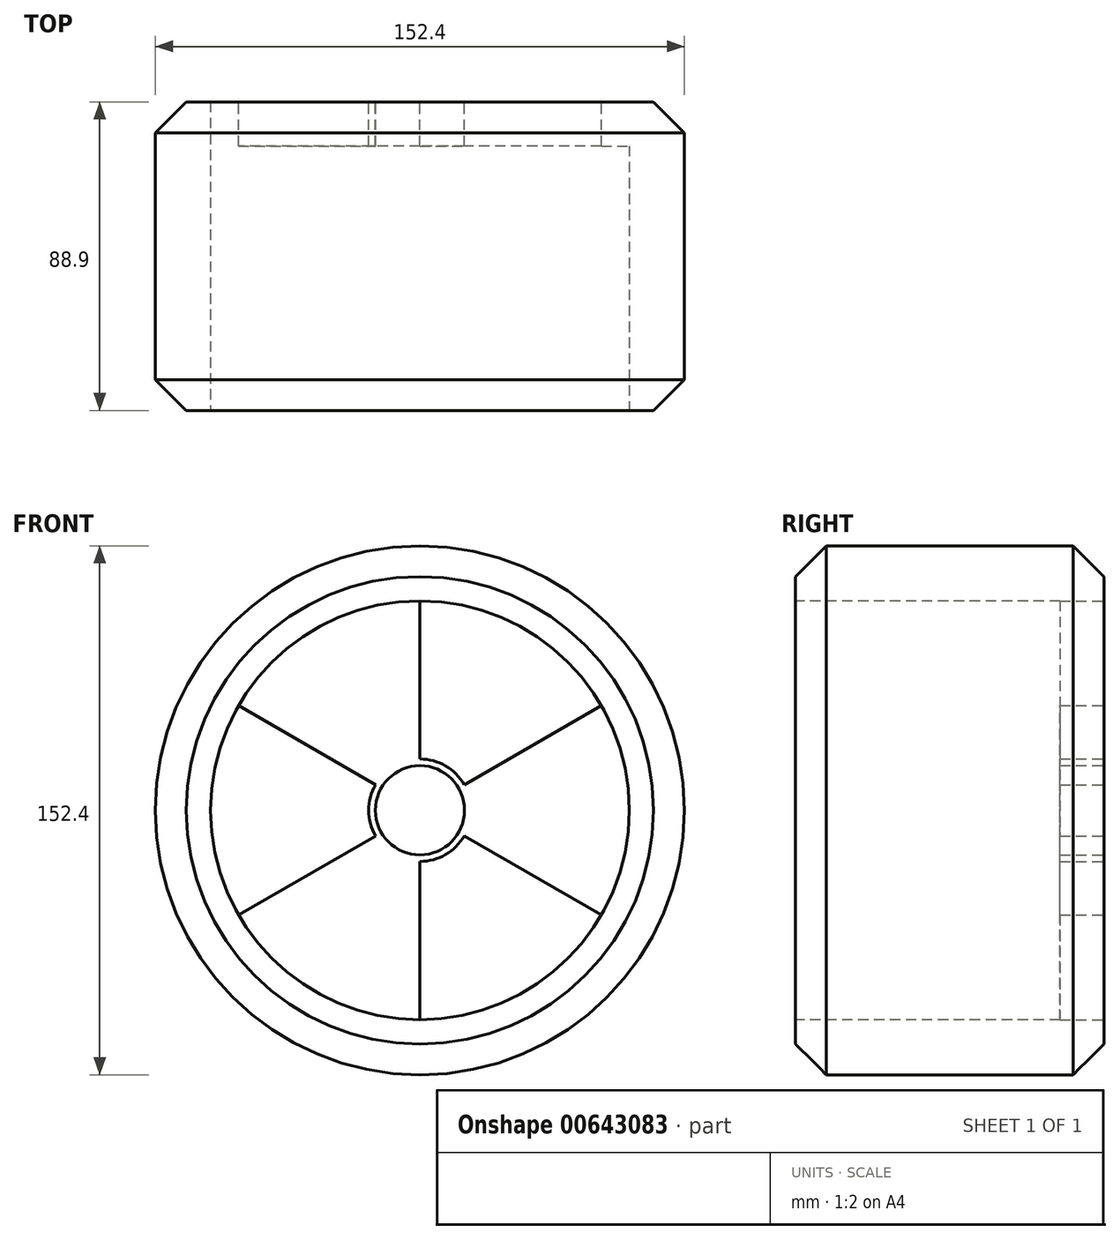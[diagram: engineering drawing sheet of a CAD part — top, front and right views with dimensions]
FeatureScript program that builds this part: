
annotation { "Feature Type Name" : "Feature", "Feature Type Description" : "" }
export const myFeature = defineFeature(function(context is Context, id is Id, definition is map)
    precondition{}
    {
        {
            var Q0;
            Q0=qCreatedBy(makeId("Front.planeOp"),FACE);
            var sketch = newSketch(context, id + "F0", { "sketchPlane" : qUnion([Q0])});
            skCircle(sketch, "E0", {"center": v(0, 0) * mm, "radius": 76.2 * mm});
            skSolve(sketch);
        }
        {
            var Q0;
            Q0=makeQuery(id+"F0.imprint","IMPRINT",FACE,{"disambiguationData":[TD([[makeQuery(id+"F0.imprint","IMPRINT",EDGE,{"derivedFrom":sQuery(id+"F0.wireOp",EDGE,"E0")}),1.0]])]});
            extrude(context, id + "F1", {"entities" : qUnion([Q0]), "depth" : 88.9 * mm, "offsetDistance" : 25.4 * mm});
        }
        {
            var Q0;
            Q0=makeQuery(id+"F1.opExtrude","CAP_FACE",FACE,{"disambiguationData":[OSD([sQuery(id+"F0.wireOp",EDGE,"E0")])],"isStart":false});
            var sketch = newSketch(context, id + "F2", { "sketchPlane" : qUnion([Q0])});
            skCircle(sketch, "E1", {"center": v(0, 0) * mm, "radius": 60.33 * mm});
            skSolve(sketch);
        }
        {
            var Q0;
            Q0=makeQuery(id+"F2.imprint","IMPRINT",FACE,{"disambiguationData":[TD([[makeQuery(id+"F2.imprint","IMPRINT",EDGE,{"derivedFrom":sQuery(id+"F2.wireOp",EDGE,"E1")}),1.0]])]});
            extrude(context, id + "F3", {"entities" : qUnion([Q0]), "operationType" : NewBodyOperationType.REMOVE, "oppositeDirection" : true, "depth" : 76.2 * mm, "offsetDistance" : 25.4 * mm});
        }
        {
            var Q0;
            Q0=makeQuery(id+"F1.opExtrude","CAP_FACE",FACE,{"disambiguationData":[OSD([sQuery(id+"F0.wireOp",EDGE,"E0")])],"isStart":true});
            var sketch = newSketch(context, id + "F4", { "sketchPlane" : qUnion([Q0])});
            skCircle(sketch, "E2", {"center": v(0, 0) * mm, "radius": 12.84 * mm});
            skSolve(sketch);
        }
        {
            var Q0;
            Q0=makeQuery(id+"F4.imprint","IMPRINT",FACE,{"disambiguationData":[TD([[makeQuery(id+"F4.imprint","IMPRINT",EDGE,{"derivedFrom":sQuery(id+"F4.wireOp",EDGE,"E2")}),1.0]])]});
            extrude(context, id + "F5", {"entities" : qUnion([Q0]), "operationType" : NewBodyOperationType.REMOVE, "oppositeDirection" : true, "depth" : 25.4 * mm, "offsetDistance" : 25.4 * mm});
        }
        {
            var Q0;
            Q0=makeQuery(id+"F1.opExtrude","CAP_FACE",FACE,{"disambiguationData":[OSD([sQuery(id+"F0.wireOp",EDGE,"E0")])],"isStart":true});
            var sketch = newSketch(context, id + "F6", { "sketchPlane" : qUnion([Q0])});
            skSolve(sketch);
        }
        {
            var Q0;
            Q0=makeQuery(id+"F6.imprint","IMPRINT",FACE,{"disambiguationData":[TD([[makeQuery(id+"F6.imprint","IMPRINT",EDGE,{"derivedFrom":makeQuery(id+"F1.opExtrude","CAP_EDGE",EDGE,{"disambiguationData":[OSD([sQuery(id+"F0.wireOp",EDGE,"E0")])],"isStart":true})}),-1.0]])]});
            var sketch = newSketch(context, id + "F7", { "sketchPlane" : qUnion([Q0])});
            skCircle(sketch, "E3", {"center": v(0, 0) * mm, "radius": 60.33 * mm});
            skPoint(sketch, "E4", {"position": v(0, 60.33) * mm});
            skPoint(sketch, "E5.1.0", {"position": v(-52.24, -30.16) * mm});
            skPoint(sketch, "E5.2.0", {"position": v(52.24, -30.16) * mm});
            skPoint(sketch, "E6", {"position": v(0, -60.33) * mm});
            skPoint(sketch, "E7.1.0", {"position": v(52.24, 30.16) * mm});
            skPoint(sketch, "E7.2.0", {"position": v(-52.24, 30.16) * mm});
            skCircle(sketch, "E8", {"center": v(0, 0) * mm, "radius": 12.84 * mm});
            skLineSegment(sketch, "E9", {"start": v(0, 14.75) * mm, "end": v(0, 60.33) * mm});
            skLineSegment(sketch, "E10", {"start": v(12.78, 7.38) * mm, "end": v(52.24, 30.16) * mm});
            skLineSegment(sketch, "E11", {"start": v(12.78, -7.38) * mm, "end": v(52.24, -30.16) * mm});
            skLineSegment(sketch, "E12", {"start": v(0, -14.75) * mm, "end": v(0, -60.33) * mm});
            skLineSegment(sketch, "E13", {"start": v(-12.78, -7.38) * mm, "end": v(-52.24, -30.16) * mm});
            skLineSegment(sketch, "E14", {"start": v(-12.78, 7.38) * mm, "end": v(-52.24, 30.16) * mm});
            skCircle(sketch, "E15", {"center": v(0, 0) * mm, "radius": 14.75 * mm});
            skSolve(sketch);
        }
        {
            var Q0;
            {var subQ0=sQuery(id+"F7.wireOp",EDGE,"E9");Q0=makeQuery(id+"F7.imprint","IMPRINT",FACE,{"disambiguationData":[TD([[makeQuery(id+"F7.imprint","IMPRINT",EDGE,{"derivedFrom":subQ0}),1.0]])]});}
            var Q1;
            {var subQ0=sQuery(id+"F7.wireOp",EDGE,"E10");Q1=makeQuery(id+"F7.imprint","IMPRINT",FACE,{"disambiguationData":[TD([[makeQuery(id+"F7.imprint","IMPRINT",EDGE,{"derivedFrom":subQ0}),-1.0]])]});}
            var Q2;
            {var subQ0=sQuery(id+"F7.wireOp",EDGE,"E12");Q2=makeQuery(id+"F7.imprint","IMPRINT",FACE,{"disambiguationData":[TD([[makeQuery(id+"F7.imprint","IMPRINT",EDGE,{"derivedFrom":subQ0}),-1.0]])]});}
            extrude(context, id + "F8", {"entities" : qUnion([Q0, Q1, Q2]), "operationType" : NewBodyOperationType.REMOVE, "oppositeDirection" : true, "depth" : 25.4 * mm, "offsetDistance" : 25.4 * mm});
        }
        {
            var Q0;
            Q0=makeQuery(id+"F1.opExtrude","CAP_EDGE",EDGE,{"disambiguationData":[OSD([sQuery(id+"F0.wireOp",EDGE,"E0")])],"isStart":true});
            chamfer(context, id + "F9", {"entities" : qUnion([Q0]), "width" : 8.9 * mm, "tangentPropagation" : true});
        }
        {
            var Q0;
            Q0=makeQuery(id+"F1.opExtrude","CAP_EDGE",EDGE,{"disambiguationData":[OSD([sQuery(id+"F0.wireOp",EDGE,"E0")])],"isStart":false});
            chamfer(context, id + "F10", {"entities" : qUnion([Q0]), "width" : 8.9 * mm, "tangentPropagation" : true});
        }
    });
